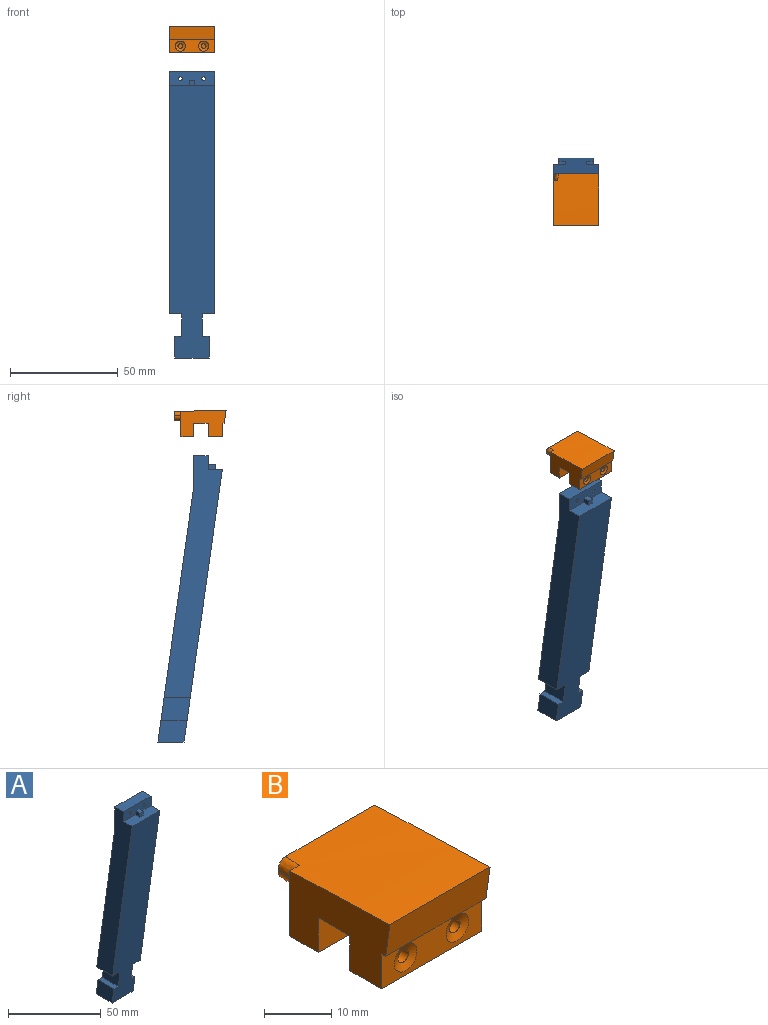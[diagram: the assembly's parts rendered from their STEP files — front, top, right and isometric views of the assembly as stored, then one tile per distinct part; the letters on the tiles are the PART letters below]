
ASSEMBLY  parts=2 mates=1
PART A: 23 faces, bbox 21x29.9x133 mm
  f0: plane 21x6.62mm, normal (0,0,1), area 130.7mm2, adj f12,f13,f14,f15,f19,f20,f21
  f1: plane 118.61x21mm, normal (0,0.99,0.14), area 2344mm2, adj f2,f3,f4,f5,f6,f7,f8,f9
  f2: plane 12.12x5.7mm, normal (0,0,-1), area 69.1mm2, adj f1,f3,f12,f14
  f3: plane 13.59x10.5mm, normal (1,0,0), area 127.2mm2, adj f1,f2,f4,f12
  f4: plane 12.12x3.2mm, normal (0,0,1), area 38.8mm2, adj f1,f3,f5,f12
  f5: plane 13.52x10mm, normal (1,0,0), area 121.2mm2, adj f1,f4,f6,f12
  f6: plane 16x12.12mm, normal (0,0,-1), area 193.9mm2, adj f1,f5,f7,f12
  f7: plane 13.52x10mm, normal (-1,0,0), area 121.2mm2, adj f1,f6,f8,f12
  f8: plane 12.12x3.2mm, normal (0,0,1), area 38.8mm2, adj f1,f7,f9,f12
  f9: plane 13.59x10.5mm, normal (-1,0,0), area 127.2mm2, adj f1,f8,f10,f12
  f10: plane 12.12x5.7mm, normal (0,0,-1), area 69.1mm2, adj f1,f9,f12,f13
  f11: plane 21x14.35mm, normal (0,1,0), area 296.5mm2, adj f1,f13,f14,f16,f17,f18
  f12: plane 126.61x21mm, normal (0,-0.99,-0.14), area 2513.6mm2, adj f0,f2,f3,f4,f5,f6,f7,f8
  f13: plane 112.46x27.03mm, normal (-1,0,0), area 1332.4mm2, adj f0,f1,f10,f11,f12,f15,f16
  f14: plane 112.46x27.03mm, normal (1,0,0), area 1332.4mm2, adj f0,f1,f2,f11,f12,f15,f16
  f15: plane 21x6.35mm, normal (0,-1,0), area 122.2mm2, adj f0,f13,f14,f16,f17,f18,f20,f21
  f16: plane 21x6.62mm, normal (0,0,1), area 139mm2, adj f11,f13,f14,f15
  f17: cylinder r=0.88mm len=6.62mm, axis (0,-1,0), area 36.4mm2, adj f11,f15
  f18: cylinder r=0.88mm len=6.62mm, axis (0,-1,0), area 36.4mm2, adj f11,f15
  f19: plane 2.51x2.51mm, normal (0,-1,0), area 6.3mm2, adj f0,f20,f21,f22
  f20: plane 3.31x2.51mm, normal (1,0,0), area 8.3mm2, adj f0,f15,f19,f22
  f21: plane 3.31x2.51mm, normal (-1,0,0), area 8.3mm2, adj f0,f15,f19,f22
  f22: plane 3.31x2.51mm, normal (0,0,1), area 8.3mm2, adj f15,f19,f20,f21
PART B: 26 faces, bbox 21x24.2x12.5 mm
  f0: plane 21x6.35mm, normal (0,1,0), area 119.3mm2, adj f1,f2,f13,f15,f18,f20,f22,f24
  f1: plane 21x12.52mm, normal (-1,0,0), area 199.9mm2, adj f0,f3,f5,f7,f12,f13,f14,f15
  f2: plane 24.19x12.52mm, normal (1,0,0), area 210.8mm2, adj f0,f3,f4,f5,f7,f8,f12,f13
  f3: cylinder r=1914.68mm len=24.19mm, axis (1,0,0), area 501.3mm2, adj f1,f2,f4,f5,f11,f12
  f4: plane 20.25x3.91mm, normal (0,1,0), area 46.4mm2, adj f2,f3,f6,f8,f9,f10,f11
  f5: plane 21x11.81mm, normal (0,1,0), area 195mm2, adj f1,f2,f3,f6,f7,f8,f9,f10
  f6: plane 12.16x3.36mm, normal (0.25,0.05,-0.97), area 40.1mm2, adj f4,f5,f8,f9
  f7: plane 21x6mm, normal (0,0,-1), area 126mm2, adj f1,f2,f5,f14
  f8: plane 6.16x3.19mm, normal (-0.38,0.05,-0.92), area 21.3mm2, adj f2,f4,f5,f6
  f9: cone r=2.16mm half-angle=3deg, axis (0,-1,0), area 10.6mm2, adj f4,f5,f6,f10
  f10: plane 3.19x0.17mm, normal (-1,0.05,0), area 0.3mm2, adj f4,f5,f9,f11
  f11: bspline ~3.51x1.84mm, area 8.2mm2, adj f3,f4,f5,f10
  f12: plane 21x6.17mm, normal (0,-0.99,-0.14), area 130.8mm2, adj f1,f2,f3,f17
  f13: plane 21x6.62mm, normal (0,0,-1), area 132mm2, adj f0,f1,f2,f16,f22,f23,f24
  f14: plane 21x6.35mm, normal (0,-1,0), area 133.3mm2, adj f1,f2,f7,f15
  f15: plane 21x6.62mm, normal (0,0,-1), area 139mm2, adj f0,f1,f2,f14
  f16: plane 21x6.35mm, normal (0,-1,0), area 97.9mm2, adj f1,f2,f13,f17,f19,f21
  f17: plane 21x0.89mm, normal (0,0,-1), area 18.7mm2, adj f1,f2,f12,f16
  f18: cylinder r=1.1mm len=6.09mm, axis (0,-1,0), area 42.1mm2, adj f0,f19
  f19: cone r=1.1mm half-angle=67.5deg, axis (0,-1,0), area 15.1mm2, adj f16,f18
  f20: cylinder r=1.1mm len=6.09mm, axis (0,-1,0), area 42.1mm2, adj f0,f21
  f21: cone r=1.1mm half-angle=67.5deg, axis (0,-1,0), area 15.1mm2, adj f16,f20
  f22: plane 2.79x2.54mm, normal (-1,0,0), area 7.1mm2, adj f0,f13,f23,f25
  f23: plane 2.54x2.54mm, normal (0,1,0), area 6.5mm2, adj f13,f22,f24,f25
  f24: plane 2.79x2.54mm, normal (1,0,0), area 7.1mm2, adj f0,f13,f23,f25
  f25: plane 2.79x2.54mm, normal (0,0,-1), area 7.1mm2, adj f0,f22,f23,f24
PLACE A t=(-35.57,-8.3,49.25)mm
PLACE B t=(-35.57,-8.3,54.24)mm
MATE slider B.f15 <-> A.f16  axis (0,0,-1) through (1.43,-4.18,70.75)mm
